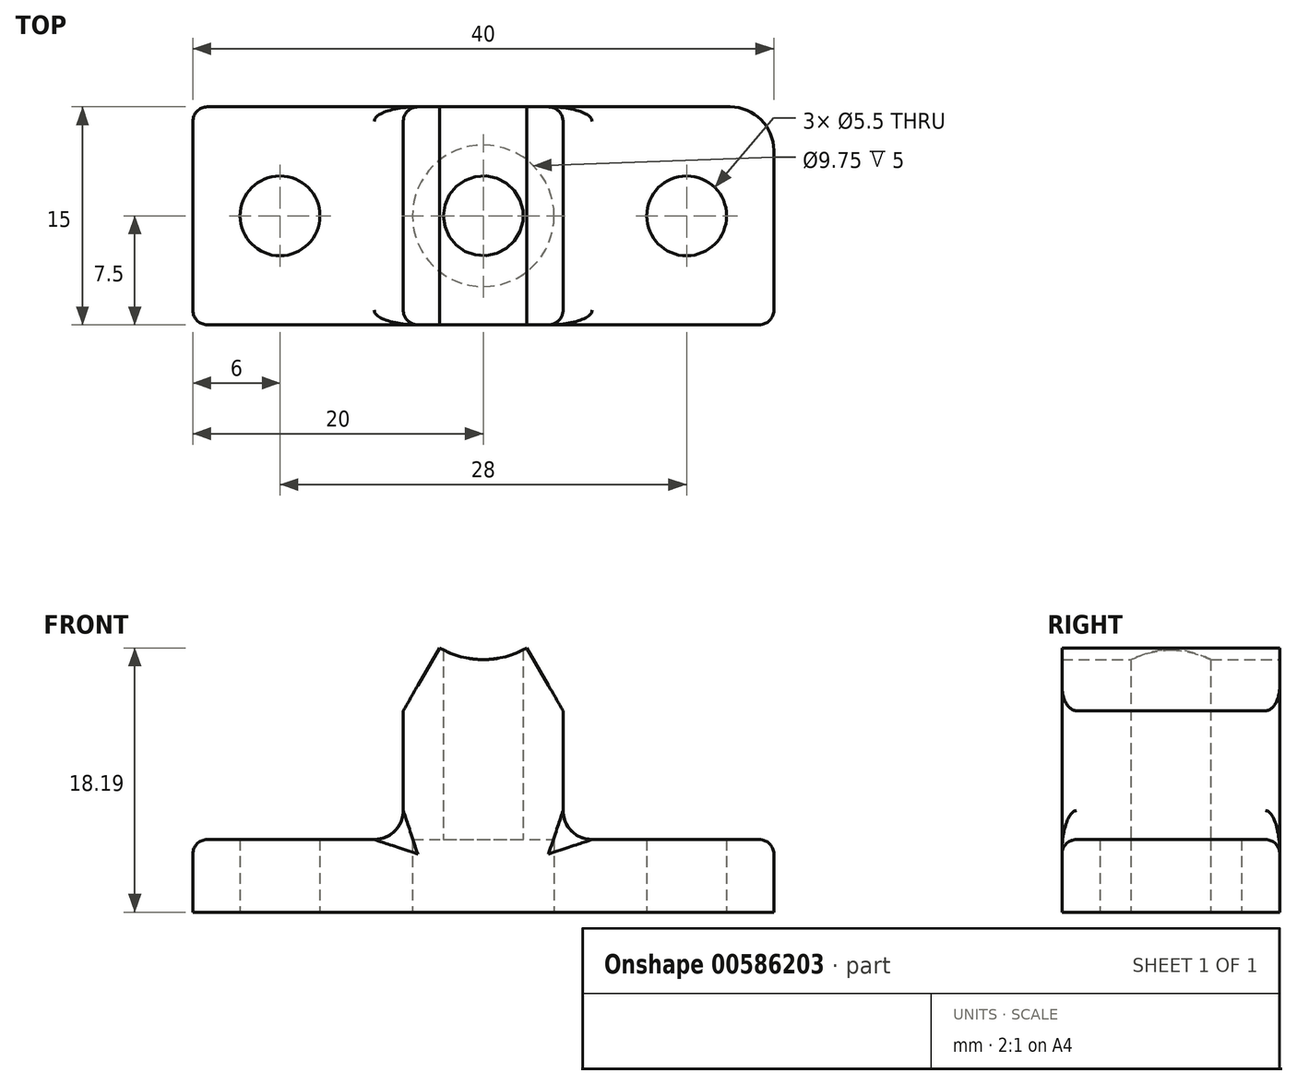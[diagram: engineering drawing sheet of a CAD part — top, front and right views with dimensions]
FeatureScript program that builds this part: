
annotation { "Feature Type Name" : "Feature", "Feature Type Description" : "" }
export const myFeature = defineFeature(function(context is Context, id is Id, definition is map)
    precondition{}
    {
        {
            var Q0;
            Q0=qCreatedBy(makeId("Front.planeOp"),FACE);
            var sketch = newSketch(context, id + "F0", { "sketchPlane" : qUnion([Q0])});
            skLineSegment(sketch, "E0", {"start": v(0, 0) * mm, "end": v(20, 0) * mm});
            skLineSegment(sketch, "E1", {"start": v(20, 0) * mm, "end": v(20, 5) * mm});
            skArc(sketch, "E2", {"start": v(-3.01, 18.2) * mm, "mid": v(-0.01, 17.4) * mm, "end": v(2.99, 18.2) * mm});
            skLineSegment(sketch, "E3", {"start": v(2.99, 18.2) * mm, "end": v(5.49, 13.86) * mm});
            skLineSegment(sketch, "E4", {"start": v(0, 0) * mm, "end": v(-20, 0) * mm});
            skLineSegment(sketch, "E5", {"start": v(-20, 0) * mm, "end": v(-20, 5) * mm});
            skLineSegment(sketch, "E6", {"start": v(-20, 5) * mm, "end": v(-5.51, 5) * mm});
            skLineSegment(sketch, "E7", {"start": v(-3.01, 18.2) * mm, "end": v(-5.51, 13.86) * mm});
            skLineSegment(sketch, "E8.trimOffspring", {"start": v(5.49, 5) * mm, "end": v(20, 5) * mm});
            skLineSegment(sketch, "E9", {"start": v(5.49, 5) * mm, "end": v(5.49, 13.86) * mm});
            skLineSegment(sketch, "E10", {"start": v(-5.51, 5) * mm, "end": v(-5.51, 13.86) * mm});
            skSolve(sketch);
        }
        {
            var Q0;
            Q0=makeQuery(id+"F0.imprint","IMPRINT",FACE,{"disambiguationData":[TD([[makeQuery(id+"F0.imprint","IMPRINT",EDGE,{"derivedFrom":sQuery(id+"F0.wireOp",EDGE,"E0")}),1.0]])]});
            extrude(context, id + "F1", {"entities" : qUnion([Q0]), "endBound" : BoundingType.SYMMETRIC, "depth" : 15 * mm, "offsetDistance" : 25 * mm});
        }
        {
            var Q0;
            Q0=makeQuery(id+"F1.opExtrude","SWEPT_FACE",FACE,{"disambiguationData":[OSD([sQuery(id+"F0.wireOp",EDGE,"E0"),sQuery(id+"F0.wireOp",EDGE,"E4")])]});
            var sketch = newSketch(context, id + "F2", { "sketchPlane" : qUnion([Q0])});
            skCircle(sketch, "E11", {"center": v(0, 0) * mm, "radius": 1.8 * mm});
            skLineSegment(sketch, "E12", {"start": v(-20, 0) * mm, "end": v(-14, 0) * mm});
            skPoint(sketch, "E12.endSnap0", {"position": v(-20, 0) * mm});
            skLineSegment(sketch, "E13", {"start": v(20, 0) * mm, "end": v(14, 0) * mm});
            skCircle(sketch, "E14", {"center": v(-14, 0) * mm, "radius": 3.06 * mm});
            skCircle(sketch, "E15", {"center": v(14, 0) * mm, "radius": 2.52 * mm});
            skCircle(sketch, "E16", {"center": v(14, 0) * mm, "radius": 0.76 * mm});
            skCircle(sketch, "E17", {"center": v(-14, 0) * mm, "radius": 0.9 * mm});
            skSolve(sketch);
        }
        {
            var Q0;
            Q0=sQuery(id+"F2.wireOp",VERTEX,"E11.center");
            var Q1;
            Q1=makeQuery(id+"F1.opExtrude","SWEPT_BODY",BODY,{"disambiguationData":[OSD([sQuery(id+"F0.wireOp",EDGE,"E0"),sQuery(id+"F0.wireOp",EDGE,"E1"),sQuery(id+"F0.wireOp",EDGE,"E2"),sQuery(id+"F0.wireOp",EDGE,"E3"),sQuery(id+"F0.wireOp",EDGE,"E4"),sQuery(id+"F0.wireOp",EDGE,"E5"),sQuery(id+"F0.wireOp",EDGE,"E6"),sQuery(id+"F0.wireOp",EDGE,"E7"),sQuery(id+"F0.wireOp",EDGE,"E8.trimOffspring"),sQuery(id+"F0.wireOp",EDGE,"E9"),sQuery(id+"F0.wireOp",EDGE,"E10")])]});
            hole(context, id + "F3", {"style" : HoleStyle.C_BORE, "endStyle" : HoleEndStyle.THROUGH, "standardTappedOrClearance" : lookupTablePath({ "standard" : "ISO", "fit" : "Normal", "size" : "M5", "type" : "Clearance" }), "standardBlindInLast" : lookupTablePath({ "fit" : "Standard", "standard" : "ISO", "size" : "M5", "type" : "Clearance" }), "holeDiameter" : 5.5 * mm, "cBoreDiameter" : 9.75 * mm, "cBoreDepth" : 5 * mm, "majorDiameter" : 5 * mm, "isTappedThrough" : true, "tappedDepth" : 12 * mm, "tapClearance" : 3, "startFromSketch" : true, "locations" : qUnion([Q0]), "scope" : qUnion([Q1])});
        }
        {
            var Q0;
            Q0=sQuery(id+"F2.wireOp",VERTEX,"E13.end");
            var Q1;
            Q1=sQuery(id+"F2.wireOp",VERTEX,"E14.center");
            var Q2;
            Q2=makeQuery(id+"F1.opExtrude","SWEPT_BODY",BODY,{"disambiguationData":[OSD([sQuery(id+"F0.wireOp",EDGE,"E0"),sQuery(id+"F0.wireOp",EDGE,"E1"),sQuery(id+"F0.wireOp",EDGE,"E2"),sQuery(id+"F0.wireOp",EDGE,"E3"),sQuery(id+"F0.wireOp",EDGE,"E4"),sQuery(id+"F0.wireOp",EDGE,"E5"),sQuery(id+"F0.wireOp",EDGE,"E6"),sQuery(id+"F0.wireOp",EDGE,"E7"),sQuery(id+"F0.wireOp",EDGE,"E8.trimOffspring"),sQuery(id+"F0.wireOp",EDGE,"E9"),sQuery(id+"F0.wireOp",EDGE,"E10")])]});
            hole(context, id + "F4", {"style" : HoleStyle.SIMPLE, "endStyle" : HoleEndStyle.THROUGH, "holeDiameter" : 5.5 * mm, "majorDiameter" : 5 * mm, "isTappedThrough" : true, "tappedDepth" : 12 * mm, "tapClearance" : 3, "startFromSketch" : true, "locations" : qUnion([Q0, Q1]), "scope" : qUnion([Q2])});
        }
        {
            var Q0;
            Q0=makeQuery(id+"F1.opExtrude","CAP_EDGE",EDGE,{"disambiguationData":[OSD([sQuery(id+"F0.wireOp",EDGE,"E1")])],"isStart":false});
            var Q1;
            Q1=makeQuery(id+"F1.opExtrude","CAP_EDGE",EDGE,{"disambiguationData":[OSD([sQuery(id+"F0.wireOp",EDGE,"E5")])],"isStart":true});
            var Q2;
            Q2=makeQuery(id+"F1.opExtrude","CAP_EDGE",EDGE,{"disambiguationData":[OSD([sQuery(id+"F0.wireOp",EDGE,"E5")])],"isStart":false});
            var Q3;
            Q3=makeQuery(id+"F1.opExtrude","CAP_EDGE",EDGE,{"disambiguationData":[OSD([sQuery(id+"F0.wireOp",EDGE,"E9")])],"isStart":false});
            var Q4;
            Q4=makeQuery(id+"F1.opExtrude","CAP_EDGE",EDGE,{"disambiguationData":[OSD([sQuery(id+"F0.wireOp",EDGE,"E10")])],"isStart":false});
            var Q5;
            Q5=makeQuery(id+"F1.opExtrude","CAP_EDGE",EDGE,{"disambiguationData":[OSD([sQuery(id+"F0.wireOp",EDGE,"E9")])],"isStart":true});
            var Q6;
            Q6=makeQuery(id+"F1.opExtrude","CAP_EDGE",EDGE,{"disambiguationData":[OSD([sQuery(id+"F0.wireOp",EDGE,"E10")])],"isStart":true});
            var Q7;
            Q7=makeQuery(id+"F1.opExtrude","CAP_EDGE",EDGE,{"disambiguationData":[OSD([sQuery(id+"F0.wireOp",EDGE,"E6")])],"isStart":false});
            var Q8;
            Q8=makeQuery(id+"F1.opExtrude","SWEPT_EDGE",EDGE,{"disambiguationData":[OSD([sQuery(id+"F0.wireOp",EDGE,"E5"),sQuery(id+"F0.wireOp",EDGE,"E6")])]});
            var Q9;
            Q9=makeQuery(id+"F1.opExtrude","CAP_EDGE",EDGE,{"disambiguationData":[OSD([sQuery(id+"F0.wireOp",EDGE,"E6")])],"isStart":true});
            var Q10;
            Q10=makeQuery(id+"F1.opExtrude","CAP_EDGE",EDGE,{"disambiguationData":[OSD([sQuery(id+"F0.wireOp",EDGE,"E8.trimOffspring")])],"isStart":false});
            var Q11;
            Q11=makeQuery(id+"F1.opExtrude","SWEPT_EDGE",EDGE,{"disambiguationData":[OSD([sQuery(id+"F0.wireOp",EDGE,"E1"),sQuery(id+"F0.wireOp",EDGE,"E8.trimOffspring")])]});
            var Q12;
            Q12=makeQuery(id+"F1.opExtrude","CAP_EDGE",EDGE,{"disambiguationData":[OSD([sQuery(id+"F0.wireOp",EDGE,"E8.trimOffspring")])],"isStart":true});
            fillet(context, id + "F5", {"entities" : qUnion([Q0, Q1, Q2, Q3, Q4, Q5, Q6, Q7, Q8, Q9, Q10, Q11, Q12]), "radius" : 1 * mm, "tangentPropagation" : true, "allowEdgeOverflow" : false});
        }
        {
            var Q0;
            Q0=makeQuery(id+"F1.opExtrude","SWEPT_EDGE",EDGE,{"disambiguationData":[OSD([sQuery(id+"F0.wireOp",EDGE,"E6"),sQuery(id+"F0.wireOp",EDGE,"E10")])]});
            var Q1;
            Q1=makeQuery(id+"F1.opExtrude","SWEPT_EDGE",EDGE,{"disambiguationData":[OSD([sQuery(id+"F0.wireOp",EDGE,"E8.trimOffspring"),sQuery(id+"F0.wireOp",EDGE,"E9")])]});
            fillet(context, id + "F6", {"entities" : qUnion([Q0, Q1]), "radius" : 2 * mm, "tangentPropagation" : true, "allowEdgeOverflow" : false});
        }
        {
            var Q0;
            Q0=makeQuery(id+"F1.opExtrude","CAP_EDGE",EDGE,{"disambiguationData":[OSD([sQuery(id+"F0.wireOp",EDGE,"E1")])],"isStart":true});
            fillet(context, id + "F7", {"entities" : qUnion([Q0]), "radius" : 3 * mm, "tangentPropagation" : true, "allowEdgeOverflow" : false});
        }
    });
